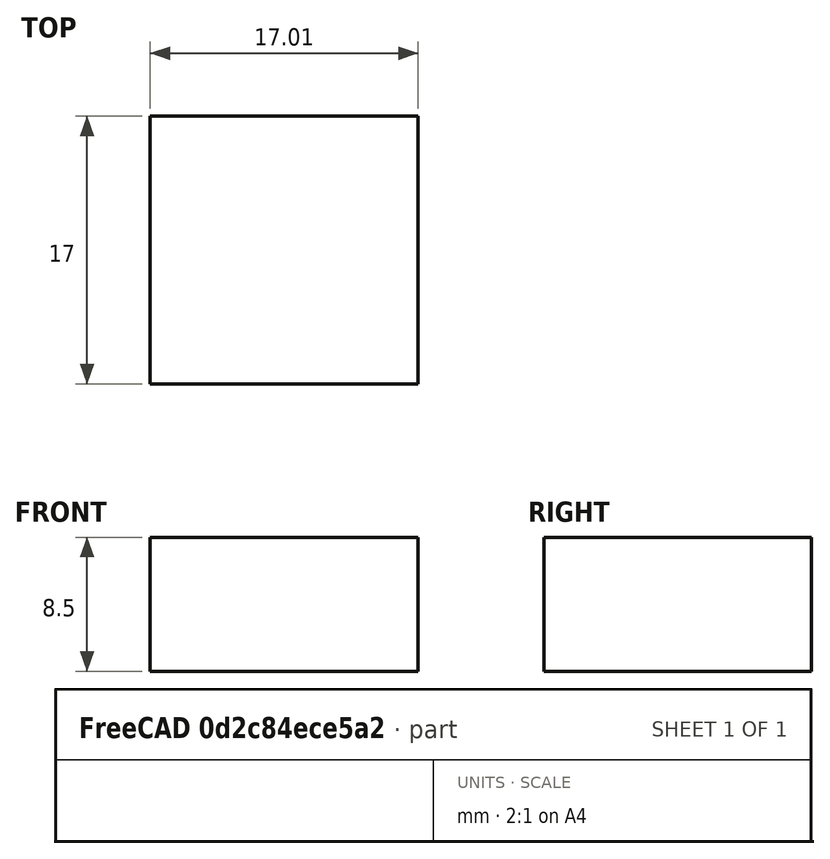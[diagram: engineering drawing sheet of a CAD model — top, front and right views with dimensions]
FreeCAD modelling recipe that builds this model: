
FCSTD DOCUMENT  (FreeCAD 0.19R24291 (Git))
Label: DGH105Q5R5
License: All rights reserved
LicenseURL: http://en.wikipedia.org/wiki/All_rights_reserved
objects: Sketcher::SketchObject×1, PartDesign::Pad×1, PartDesign::Body×1
note: 4 computed .brp shape members not serialized (recipe doc carries the construction recipe); baked Part::Feature solids carry a one-line shape summary decoded from their .brp

FEATURE [Sketcher::SketchObject] Sketch
  FullyConstrained = false
  MapMode = 5
  Support = -> [XY_Plane]
  sketch-geometry (4):
    g0: LineSegment StartX=0 StartY=0 StartZ=0 EndX=17.0121 EndY=0 EndZ=0
    g1: LineSegment StartX=17.0121 StartY=0 StartZ=0 EndX=17.0121 EndY=-17.0033 EndZ=0
    g2: LineSegment StartX=17.0121 StartY=-17.0033 StartZ=0 EndX=0 EndY=-17.0033 EndZ=0
    g3: LineSegment StartX=0 StartY=-17.0033 StartZ=0 EndX=0 EndY=0 EndZ=0
  constraints (9):
    c: Coincident(g0,g1)
    c: Coincident(g1,g2)
    c: Coincident(g2,g3)
    c: Coincident(g3,g0)
    c: Horizontal(g0)
    c: Horizontal(g2)
    c: Vertical(g1)
    c: Vertical(g3)
    c: Coincident(g0,g-1)
FEATURE [PartDesign::Pad] Pad
  Direction = (1,1,1)
  Length = 8.5
  Length2 = 100
  Profile = -> Sketch
  Type = 0
FEATURE [PartDesign::Body] Body
  Group = -> [Sketch,Pad]
  Origin = -> Origin
  Tip = -> Pad
